# Revit family: Window-Awning-Kolbe_VistaLuxe-Accent_Style
name_source: partatom
category: Windows
revit_build: Autodesk Revit Architecture 2012 (Build: 20110916_2132(x64)
units: mm (PartAtom-declared; Revit-internal decimal feet)

## types (1)
- Window-Awning-Kolbe_VistaLuxe-Accent_Style
    # of Horizontal Lites = 3
    # of Horizontal Mullions = 2
    # of Vertical Lites = 1
    # of Vertical Mullions = 2
    04 CSI = 08 52 00
    95 CSI = 08550
    Default Sill Height = 3' - 0"
    Description = Kolbe VistaLuxe Awning Accent Style
    Exterior Jamb and Trim Finish = Paint-Kolbe-Slate
    Exterior Sash and Grille Finish = Paint-Kolbe-Slate
    Exterior Wall Offset = 0' - 0"
    Glass Pane Finish = Glass-Kolbe-LoE²_270
    Grille = Yes
    Grille Height = 1' - 7 9/16"
    Grille Width = 0' - 11 9/16"
    Height = 2' - 0"
    Horizontal Grid = No
    Horizontal Grid Members = Yes
    Manufacturer = Kolbe & Kolbe Millwork Co., Inc.
    Model = VLA1420
    Mullion Width = 0' - 0 5/8"
    Product Documentation Link = http://www.kolbe-kolbe.com
    Rough Height = 2' - 0 1/2"
    Rough Width = 1' - 4 1/2"
    URL = www.kolbe-kolbe.com
    Vertical Grid = No
    Vertical Grid Members = No
    Wall Closure = By host
    Width = 1' - 4"

## geometry (parser evidence)
native form markers: Blend x4, Sweep x16
no freeform markers — native parametric forms only
